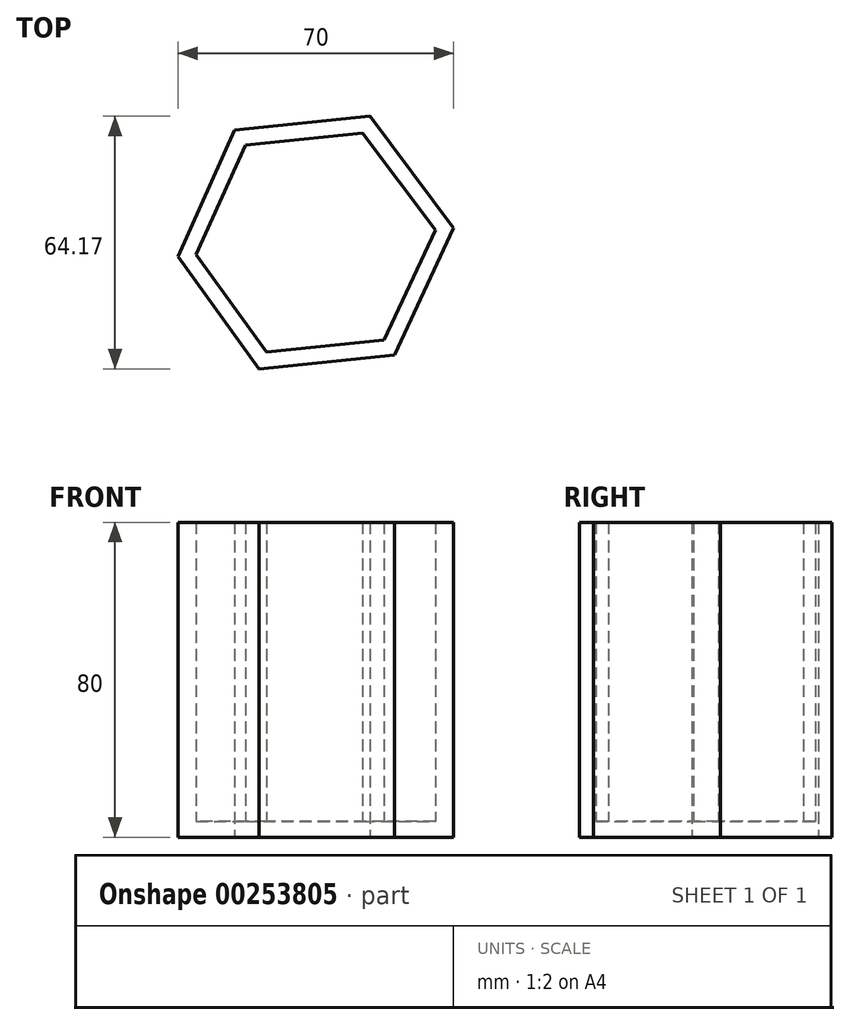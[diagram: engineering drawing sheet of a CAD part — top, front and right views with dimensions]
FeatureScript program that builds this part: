
annotation { "Feature Type Name" : "Feature", "Feature Type Description" : "" }
export const myFeature = defineFeature(function(context is Context, id is Id, definition is map)
    precondition{}
    {
        {
            var Q0;
            Q0=qCreatedBy(makeId("Top.planeOp"),FACE);
            var sketch = newSketch(context, id + "F0", { "sketchPlane" : qUnion([Q0])});
            skLineSegment(sketch, "E0.0", {"start": v(-20.62, 28.5) * mm, "end": v(13.76, 32.05) * mm});
            skLineSegment(sketch, "E0.1", {"start": v(13.76, 32.05) * mm, "end": v(35, 3.6) * mm});
            skLineSegment(sketch, "E0.2", {"start": v(35, 3.6) * mm, "end": v(20.01, -28.57) * mm});
            skLineSegment(sketch, "E0.3", {"start": v(20.01, -28.57) * mm, "end": v(-14.38, -32.12) * mm});
            skLineSegment(sketch, "E0.4", {"start": v(-14.38, -32.12) * mm, "end": v(-35, -3.6) * mm});
            skLineSegment(sketch, "E0.5", {"start": v(-35, -3.6) * mm, "end": v(-20.62, 28.5) * mm});
            skPoint(sketch, "E0.0.midPoint", {"position": v(-3.43, 30.28) * mm});
            skLineSegment(sketch, "E1.0", {"start": v(-12.49, -27.9) * mm, "end": v(-30.4, -3.13) * mm});
            skLineSegment(sketch, "E1.1", {"start": v(-17.92, 24.76) * mm, "end": v(11.91, 27.84) * mm});
            skLineSegment(sketch, "E1.2", {"start": v(11.91, 27.84) * mm, "end": v(30.36, 3.13) * mm});
            skLineSegment(sketch, "E1.3", {"start": v(-30.4, -3.13) * mm, "end": v(-17.92, 24.76) * mm});
            skLineSegment(sketch, "E1.4", {"start": v(30.36, 3.13) * mm, "end": v(17.34, -24.82) * mm});
            skLineSegment(sketch, "E1.5", {"start": v(17.34, -24.82) * mm, "end": v(-12.49, -27.9) * mm});
            skSolve(sketch);
        }
        {
            var Q0;
            Q0=makeQuery(id+"F0.imprint","IMPRINT",FACE,{"disambiguationData":[TD([[makeQuery(id+"F0.imprint","IMPRINT",EDGE,{"derivedFrom":sQuery(id+"F0.wireOp",EDGE,"E1.0")}),-1.0]])]});
            extrude(context, id + "F1", {"entities" : qUnion([Q0]), "depth" : 4 * mm});
        }
        {
            var Q0;
            Q0=makeQuery(id+"F0.imprint","IMPRINT",FACE,{"disambiguationData":[TD([[makeQuery(id+"F0.imprint","IMPRINT",EDGE,{"derivedFrom":sQuery(id+"F0.wireOp",EDGE,"E0.0")}),-1.0]])]});
            extrude(context, id + "F2", {"entities" : qUnion([Q0]), "operationType" : NewBodyOperationType.ADD, "depth" : 80 * mm});
        }
    });
